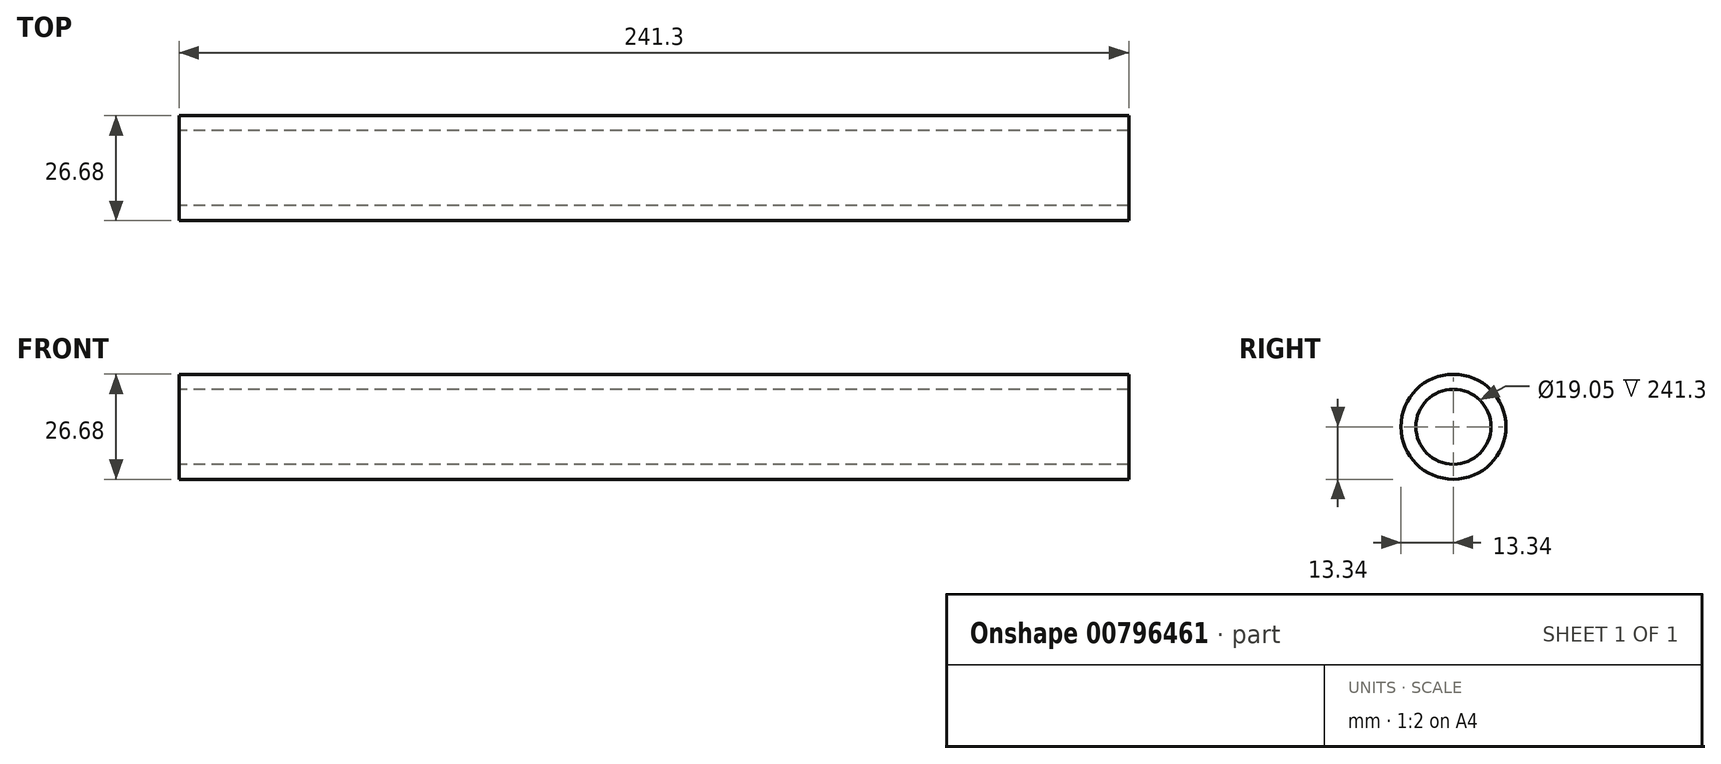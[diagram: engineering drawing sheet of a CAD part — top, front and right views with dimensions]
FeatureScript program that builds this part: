
annotation { "Feature Type Name" : "Feature", "Feature Type Description" : "" }
export const myFeature = defineFeature(function(context is Context, id is Id, definition is map)
    precondition{}
    {
        {
            var Q0;
            Q0=qCreatedBy(makeId("Right.planeOp"),FACE);
            var sketch = newSketch(context, id + "F0", { "sketchPlane" : qUnion([Q0])});
            skCircle(sketch, "E0", {"center": v(0, 0) * mm, "radius": 9.53 * mm});
            skCircle(sketch, "E1.0", {"center": v(0, 0) * mm, "radius": 13.33 * mm});
            skSolve(sketch);
        }
        {
            var Q0;
            Q0 = qSketchRegion(id + "F0", true);
            extrude(context, id + "F1", {"entities" : qUnion([Q0]), "depth" : 241.3 * mm, "offsetDistance" : 25.4 * mm});
        }
    });
